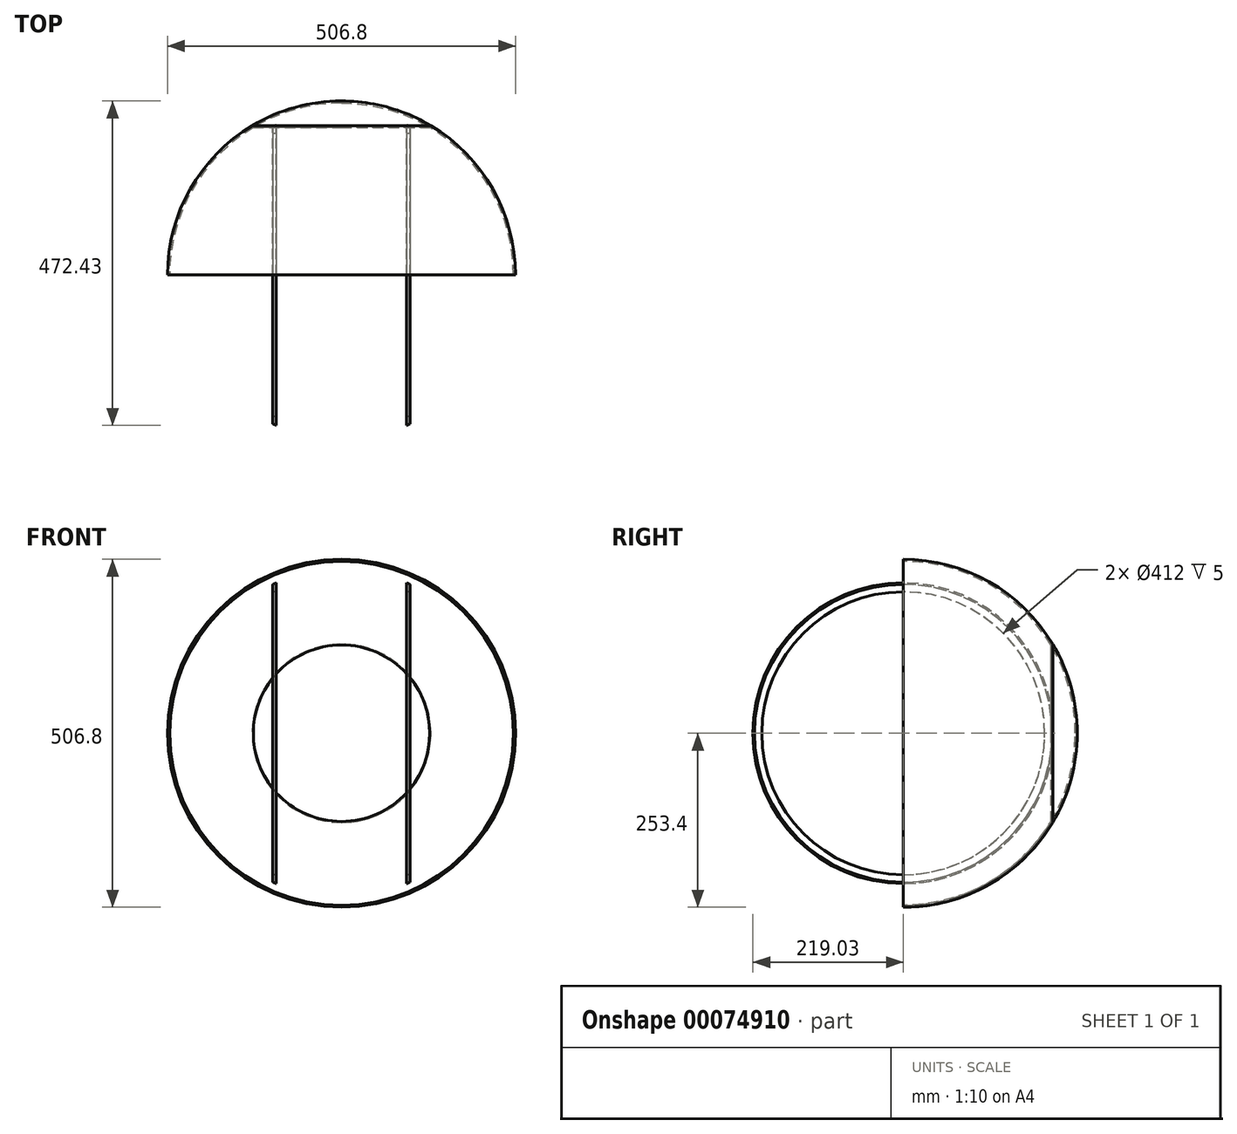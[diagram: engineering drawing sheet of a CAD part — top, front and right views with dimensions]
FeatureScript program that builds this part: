
annotation { "Feature Type Name" : "Feature", "Feature Type Description" : "" }
export const myFeature = defineFeature(function(context is Context, id is Id, definition is map)
    precondition{}
    {
        {
            var Q0;
            Q0=qCreatedBy(makeId("Top.planeOp"),FACE);
            var sketch = newSketch(context, id + "F0", { "sketchPlane" : qUnion([Q0])});
            skArc(sketch, "E0", {"start": v(-95, 225.83) * mm, "mid": v(0, 245) * mm, "end": v(95, 225.83) * mm});
            skArc(sketch, "E1", {"start": v(-100, 229.57) * mm, "mid": v(0, 250.4) * mm, "end": v(100, 229.57) * mm});
            skLineSegment(sketch, "E2", {"start": v(-100, 229.57) * mm, "end": v(-100, 206) * mm});
            skLineSegment(sketch, "E3", {"start": v(-100, 206) * mm, "end": v(-95, 206) * mm});
            skLineSegment(sketch, "E4", {"start": v(100, 229.57) * mm, "end": v(100, 206) * mm});
            skLineSegment(sketch, "E5", {"start": v(100, 206) * mm, "end": v(95, 206) * mm});
            skLineSegment(sketch, "E6", {"start": v(-95, 0) * mm, "end": v(95, 0) * mm, "construction": true});
            skLineSegment(sketch, "E7", {"start": v(-95, 206) * mm, "end": v(-95, 0) * mm, "construction": true});
            skLineSegment(sketch, "E8", {"start": v(95, 206) * mm, "end": v(95, 225.83) * mm});
            skLineSegment(sketch, "E9", {"start": v(-95, 206) * mm, "end": v(-95, 225.83) * mm});
            skLineSegment(sketch, "E10", {"start": v(95, 0) * mm, "end": v(95, 206) * mm, "construction": true});
            skPoint(sketch, "E11.positionSnap0", {"position": v(0, 225) * mm});
            skLineSegment(sketch, "E12", {"start": v(-95, 225.83) * mm, "end": v(95, 225.83) * mm, "construction": true});
            skPoint(sketch, "E13", {"position": v(0, 225.83) * mm});
            skLineSegment(sketch, "E14", {"start": v(95, 225.83) * mm, "end": v(89.8, 225.83) * mm});
            skLineSegment(sketch, "E15", {"start": v(-95, 225.83) * mm, "end": v(-89.8, 225.83) * mm});
            skLineSegment(sketch, "E16", {"start": v(-89.8, 225.83) * mm, "end": v(-89.8, 220.83) * mm});
            skLineSegment(sketch, "E17", {"start": v(-89.8, 220.83) * mm, "end": v(-85, 220.83) * mm});
            skLineSegment(sketch, "E18", {"start": v(-85, 220.83) * mm, "end": v(-85, 229.78) * mm});
            skLineSegment(sketch, "E19", {"start": v(89.8, 225.83) * mm, "end": v(89.8, 220.83) * mm});
            skLineSegment(sketch, "E20", {"start": v(89.8, 220.83) * mm, "end": v(85, 220.83) * mm});
            skLineSegment(sketch, "E21", {"start": v(85, 220.83) * mm, "end": v(85, 229.78) * mm});
            skLineSegment(sketch, "E22.bottom", {"start": v(9.04, 249.44) * mm, "end": v(-9.04, 249.44) * mm});
            skLineSegment(sketch, "E22.top", {"start": v(9.04, 245.63) * mm, "end": v(-9.04, 245.63) * mm});
            skLineSegment(sketch, "E22.left", {"start": v(9.04, 249.44) * mm, "end": v(9.04, 245.63) * mm});
            skLineSegment(sketch, "E22.right", {"start": v(-9.04, 249.44) * mm, "end": v(-9.04, 245.63) * mm});
            skPoint(sketch, "E22.middle", {"position": v(0, 247.54) * mm});
            skLineSegment(sketch, "E23.bottom", {"start": v(95, 225.83) * mm, "end": v(94, 225.83) * mm});
            skLineSegment(sketch, "E23.top", {"start": v(95, 206) * mm, "end": v(94, 206) * mm});
            skLineSegment(sketch, "E23.left", {"start": v(95, 225.83) * mm, "end": v(95, 206) * mm});
            skLineSegment(sketch, "E23.right", {"start": v(94, 225.83) * mm, "end": v(94, 206) * mm});
            skLineSegment(sketch, "E24.bottom", {"start": v(-95, 225.83) * mm, "end": v(-94, 225.83) * mm});
            skLineSegment(sketch, "E24.top", {"start": v(-95, 206) * mm, "end": v(-94, 206) * mm});
            skLineSegment(sketch, "E24.left", {"start": v(-95, 225.83) * mm, "end": v(-95, 206) * mm});
            skLineSegment(sketch, "E24.right", {"start": v(-94, 225.83) * mm, "end": v(-94, 206) * mm});
            skArc(sketch, "E25", {"start": v(-250.4, 0) * mm, "mid": v(0, 250.4) * mm, "end": v(250.4, 0) * mm});
            skArc(sketch, "E26", {"start": v(-238.74, 0) * mm, "mid": v(0, 238.74) * mm, "end": v(238.74, 0) * mm});
            skLineSegment(sketch, "E27", {"start": v(250.4, 0) * mm, "end": v(238.74, 0) * mm});
            skLineSegment(sketch, "E28", {"start": v(-250.4, 0) * mm, "end": v(-238.74, 0) * mm});
            skLineSegment(sketch, "E29", {"start": v(0, -79.52) * mm, "end": v(0, 116.69) * mm, "construction": true});
            skArc(sketch, "E30", {"start": v(130, 217.51) * mm, "mid": v(0, 253.4) * mm, "end": v(-130, 217.51) * mm});
            skPoint(sketch, "E31", {"position": v(0, 253.4) * mm});
            skLineSegment(sketch, "E32", {"start": v(130, 217.51) * mm, "end": v(128.46, 214.94) * mm});
            skLineSegment(sketch, "E33", {"start": v(-130, 217.51) * mm, "end": v(-128.46, 214.94) * mm});
            skLineSegment(sketch, "E34", {"start": v(0, 253.4) * mm, "end": v(0, 250.4) * mm});
            skArc(sketch, "E35", {"start": v(130, 217.51) * mm, "mid": v(220.4, 125.04) * mm, "end": v(253.4, 0) * mm});
            skLineSegment(sketch, "E36", {"start": v(250.4, 0) * mm, "end": v(253.4, 0) * mm});
            skLineSegment(sketch, "E37", {"start": v(0, 0) * mm, "end": v(217.51, 130) * mm, "construction": true});
            skLineSegment(sketch, "E38", {"start": v(217.51, 130) * mm, "end": v(214.94, 128.46) * mm});
            skLineSegment(sketch, "E39", {"start": v(128.46, 214.94) * mm, "end": v(0, 0) * mm, "construction": true});
            skArc(sketch, "E40", {"start": v(-130, 217.51) * mm, "mid": v(-220.4, 125.04) * mm, "end": v(-253.4, 0) * mm});
            skLineSegment(sketch, "E41", {"start": v(-253.4, 0) * mm, "end": v(-250.4, 0) * mm});
            skLineSegment(sketch, "E42", {"start": v(0, 0) * mm, "end": v(-217.51, 130) * mm, "construction": true});
            skLineSegment(sketch, "E43", {"start": v(-217.51, 130) * mm, "end": v(-214.94, 128.46) * mm});
            skSolve(sketch);
        }
        {
            var Q0;
            {var subQ0=sQuery(id+"F0.wireOp",EDGE,"E32");Q0=makeQuery(id+"F0.imprint","IMPRINT",FACE,{"disambiguationData":[TD([[makeQuery(id+"F0.imprint","IMPRINT",EDGE,{"derivedFrom":subQ0}),-1.0]])]});}
            var Q1;
            Q1=sQuery(id+"F0.wireOp",EDGE,"E29");
            revolve(context, id + "F1", {"entities" : qUnion([Q0]), "axis" : qUnion([Q1]), "revolveType" : RevolveType.FULL});
        }
        {
            var Q0;
            {var subQ0=sQuery(id+"F0.wireOp",EDGE,"E41");Q0=makeQuery(id+"F0.imprint","IMPRINT",FACE,{"disambiguationData":[TD([[makeQuery(id+"F0.imprint","IMPRINT",EDGE,{"derivedFrom":subQ0}),1.0]])]});}
            var Q1;
            {var subQ0=sQuery(id+"F0.wireOp",EDGE,"E33");Q1=makeQuery(id+"F0.imprint","IMPRINT",FACE,{"disambiguationData":[TD([[makeQuery(id+"F0.imprint","IMPRINT",EDGE,{"derivedFrom":subQ0}),-1.0]])]});}
            var Q2;
            {var subQ0=sQuery(id+"F0.wireOp",EDGE,"E32");Q2=makeQuery(id+"F0.imprint","IMPRINT",FACE,{"disambiguationData":[TD([[makeQuery(id+"F0.imprint","IMPRINT",EDGE,{"derivedFrom":subQ0}),1.0]])]});}
            var Q3;
            {var subQ0=sQuery(id+"F0.wireOp",EDGE,"E36");Q3=makeQuery(id+"F0.imprint","IMPRINT",FACE,{"disambiguationData":[TD([[makeQuery(id+"F0.imprint","IMPRINT",EDGE,{"derivedFrom":subQ0}),1.0]])]});}
            var Q4;
            Q4=sQuery(id+"F0.wireOp",EDGE,"E29");
            revolve(context, id + "F2", {"entities" : qUnion([Q0, Q1, Q2, Q3]), "axis" : qUnion([Q4]), "revolveType" : RevolveType.FULL});
        }
        {
            var Q0;
            Q0=makeQuery(id+"F0.imprint","IMPRINT",FACE,{"disambiguationData":[TD([[makeQuery(id+"F0.imprint","IMPRINT",EDGE,{"derivedFrom":sQuery(id+"F0.wireOp",EDGE,"E22.bottom")}),-1.0]])]});
            var Q1;
            {var subQ0=sQuery(id+"F0.wireOp",EDGE,"E5");Q1=makeQuery(id+"F0.imprint","IMPRINT",FACE,{"disambiguationData":[TD([[makeQuery(id+"F0.imprint","IMPRINT",EDGE,{"derivedFrom":subQ0}),-1.0]])]});}
            var Q2;
            {var subQ0=sQuery(id+"F0.wireOp",EDGE,"E3");Q2=makeQuery(id+"F0.imprint","IMPRINT",FACE,{"disambiguationData":[TD([[makeQuery(id+"F0.imprint","IMPRINT",EDGE,{"derivedFrom":subQ0}),1.0]])]});}
            var Q3;
            Q3=sQuery(id+"F0.wireOp",EDGE,"E6");
            revolve(context, id + "F3", {"entities" : qUnion([Q0, Q1, Q2]), "axis" : qUnion([Q3]), "revolveType" : RevolveType.FULL});
        }
    });
